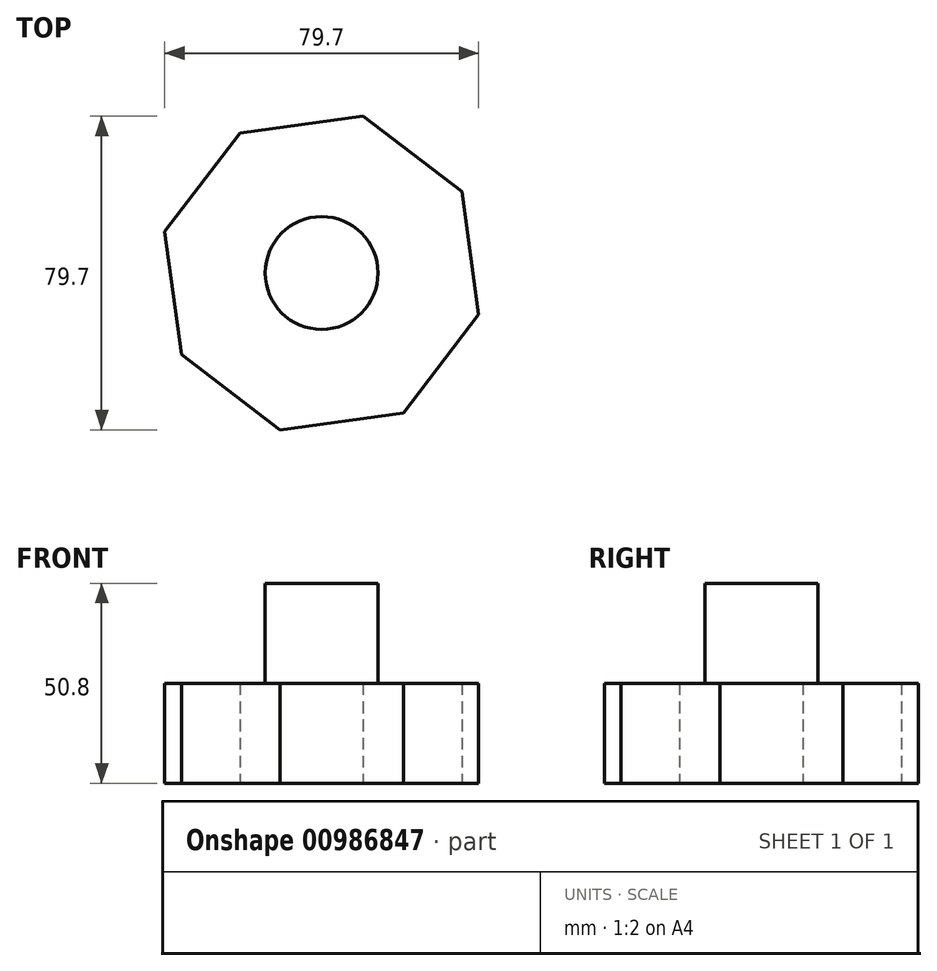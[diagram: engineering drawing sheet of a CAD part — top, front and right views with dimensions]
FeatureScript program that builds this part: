
annotation { "Feature Type Name" : "Feature", "Feature Type Description" : "" }
export const myFeature = defineFeature(function(context is Context, id is Id, definition is map)
    precondition{}
    {
        {
            var Q0;
            Q0=qCreatedBy(makeId("Top.planeOp"),FACE);
            var sketch = newSketch(context, id + "F0", { "sketchPlane" : qUnion([Q0])});
            skCircle(sketch, "E0.cCircle", {"center": v(0, 0) * mm, "radius": 38.08 * mm, "construction": true});
            skLineSegment(sketch, "E0.0", {"start": v(39.85, -10.52) * mm, "end": v(20.75, -35.62) * mm});
            skLineSegment(sketch, "E0.1", {"start": v(20.75, -35.62) * mm, "end": v(-10.52, -39.85) * mm});
            skLineSegment(sketch, "E0.2", {"start": v(-10.52, -39.85) * mm, "end": v(-35.62, -20.75) * mm});
            skLineSegment(sketch, "E0.3", {"start": v(-35.62, -20.75) * mm, "end": v(-39.85, 10.52) * mm});
            skLineSegment(sketch, "E0.4", {"start": v(-39.85, 10.52) * mm, "end": v(-20.75, 35.62) * mm});
            skLineSegment(sketch, "E0.5", {"start": v(-20.75, 35.62) * mm, "end": v(10.52, 39.85) * mm});
            skLineSegment(sketch, "E0.6", {"start": v(10.52, 39.85) * mm, "end": v(35.62, 20.75) * mm});
            skLineSegment(sketch, "E0.7", {"start": v(35.62, 20.75) * mm, "end": v(39.85, -10.52) * mm});
            skPoint(sketch, "E0.0.midPoint", {"position": v(30.3, -23.07) * mm});
            skSolve(sketch);
        }
        {
            var Q0;
            Q0=makeQuery(id+"F0.imprint","IMPRINT",FACE,{"disambiguationData":[TD([[makeQuery(id+"F0.imprint","IMPRINT",EDGE,{"derivedFrom":sQuery(id+"F0.wireOp",EDGE,"E0.0")}),-1.0]])]});
            extrude(context, id + "F1", {"entities" : qUnion([Q0]), "depth" : 25.4 * mm, "offsetDistance" : 25.4 * mm});
        }
        {
            var Q0;
            Q0=makeQuery(id+"F1.opExtrude","CAP_FACE",FACE,{"disambiguationData":[OSD([sQuery(id+"F0.wireOp",EDGE,"E0.0"),sQuery(id+"F0.wireOp",EDGE,"E0.1"),sQuery(id+"F0.wireOp",EDGE,"E0.2"),sQuery(id+"F0.wireOp",EDGE,"E0.3"),sQuery(id+"F0.wireOp",EDGE,"E0.4"),sQuery(id+"F0.wireOp",EDGE,"E0.5"),sQuery(id+"F0.wireOp",EDGE,"E0.6"),sQuery(id+"F0.wireOp",EDGE,"E0.7")])],"isStart":false});
            var sketch = newSketch(context, id + "F2", { "sketchPlane" : qUnion([Q0])});
            skCircle(sketch, "E1", {"center": v(0, 0) * mm, "radius": 14.33 * mm});
            skSolve(sketch);
        }
        {
            var Q0;
            Q0 = qSketchRegion(id + "F2", true);
            extrude(context, id + "F3", {"entities" : qUnion([Q0]), "operationType" : NewBodyOperationType.ADD, "depth" : 25.4 * mm, "offsetDistance" : 25.4 * mm});
        }
    });
